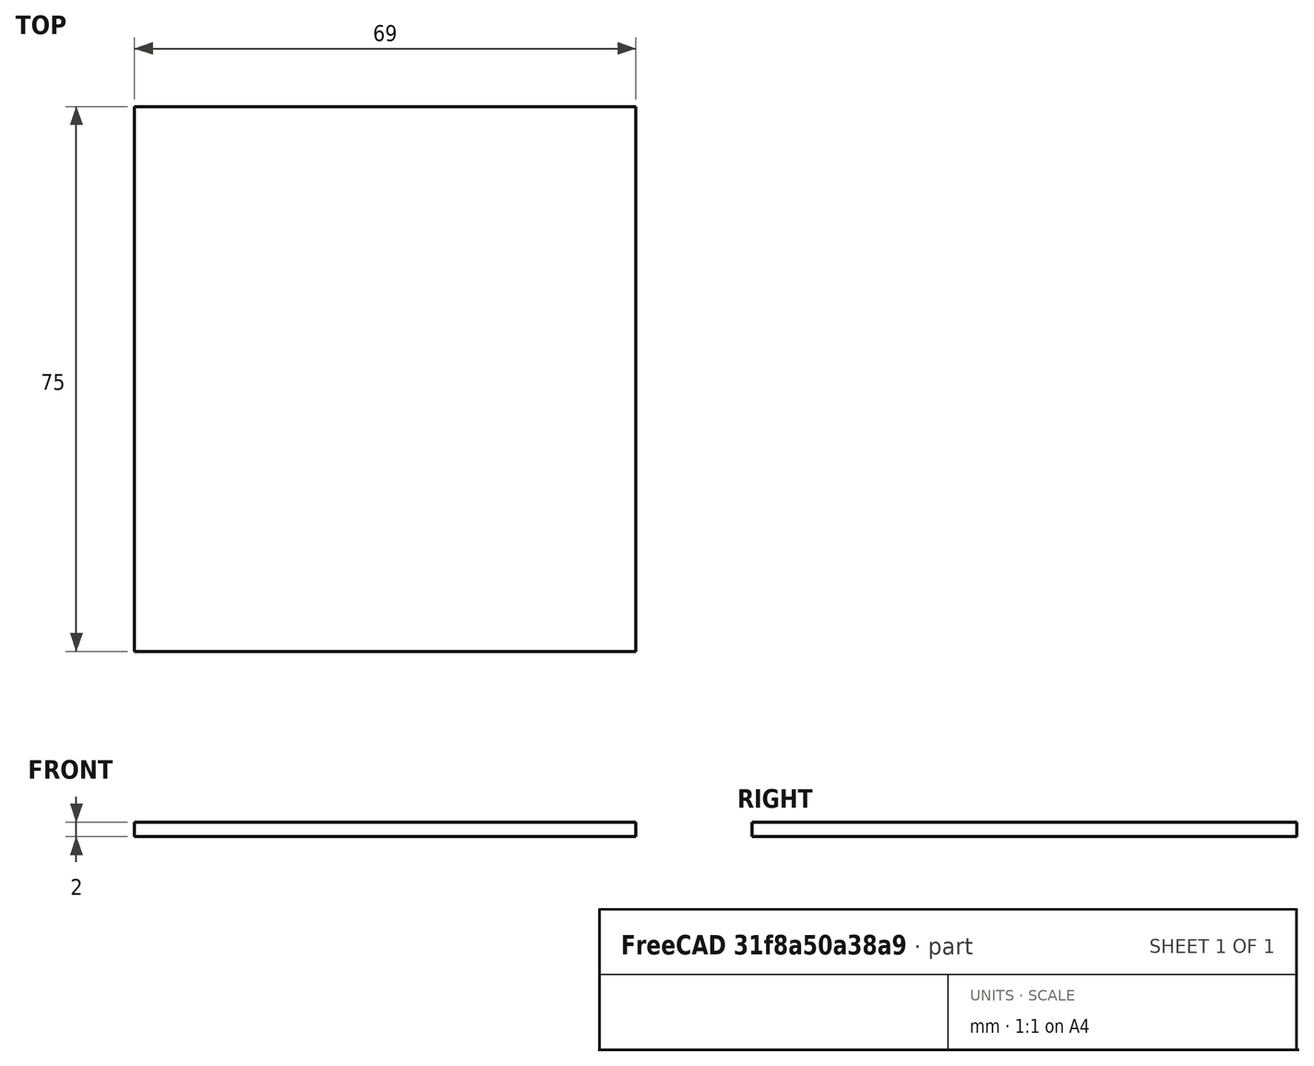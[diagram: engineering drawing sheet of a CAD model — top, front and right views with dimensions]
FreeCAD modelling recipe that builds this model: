
FCSTD DOCUMENT  (FreeCAD 1.1R40938 (Git))
Label: KEYPAD
License: All rights reserved
LicenseURL: https://en.wikipedia.org/wiki/All_rights_reserved
objects: Sketcher::SketchObject×1, PartDesign::Pad×1, PartDesign::Body×1, App::Point×1
note: 6 computed .brp shape members not serialized (recipe doc carries the construction recipe); baked Part::Feature solids carry a one-line shape summary decoded from their .brp

FEATURE [Sketcher::SketchObject] Sketch
  ArcFitTolerance = 1e-06
  AttachmentSupport = -> [XY_Plane]
  ExternalTypes = [0]
  FullyConstrained = true
  MakeInternals = false
  MapMode = 5
  sketch-geometry (4):
    g0: LineSegment StartX=-34.5 StartY=37.5 StartZ=0 EndX=-34.5 EndY=-37.5 EndZ=0
    g1: LineSegment StartX=-34.5 StartY=-37.5 StartZ=0 EndX=34.5 EndY=-37.5 EndZ=0
    g2: LineSegment StartX=34.5 StartY=-37.5 StartZ=0 EndX=34.5 EndY=37.5 EndZ=0
    g3: LineSegment StartX=34.5 StartY=37.5 StartZ=0 EndX=-34.5 EndY=37.5 EndZ=0
  constraints (11):
    c: Coincident(g0,g1)
    c: Coincident(g1,g2)
    c: Coincident(g2,g3)
    c: Coincident(g3,g0)
    c: Vertical(g0)
    c: Vertical(g2)
    c: Horizontal(g1)
    c: Horizontal(g3)
    c: Distance(g0,g2) = 69
    c: Distance(g1,g3) = 75
    c: Symmetric(g0,g1,g-1)
FEATURE [PartDesign::Pad] Pad
  Direction = (0,0,1)
  Length = 2
  Length2 = 10
  Profile = -> Sketch
  ReferenceAxis = -> Sketch [N_Axis]
  Refine = true
  Suppressed = false
  Type = 0
FEATURE [PartDesign::Body] Body
  AllowCompound = false
  Group = -> [Sketch,Pad]
  Origin = -> Origin
  Tip = -> Pad
FEATURE [App::Point] Origin001  label="Початок координат"
  Role = Origin
